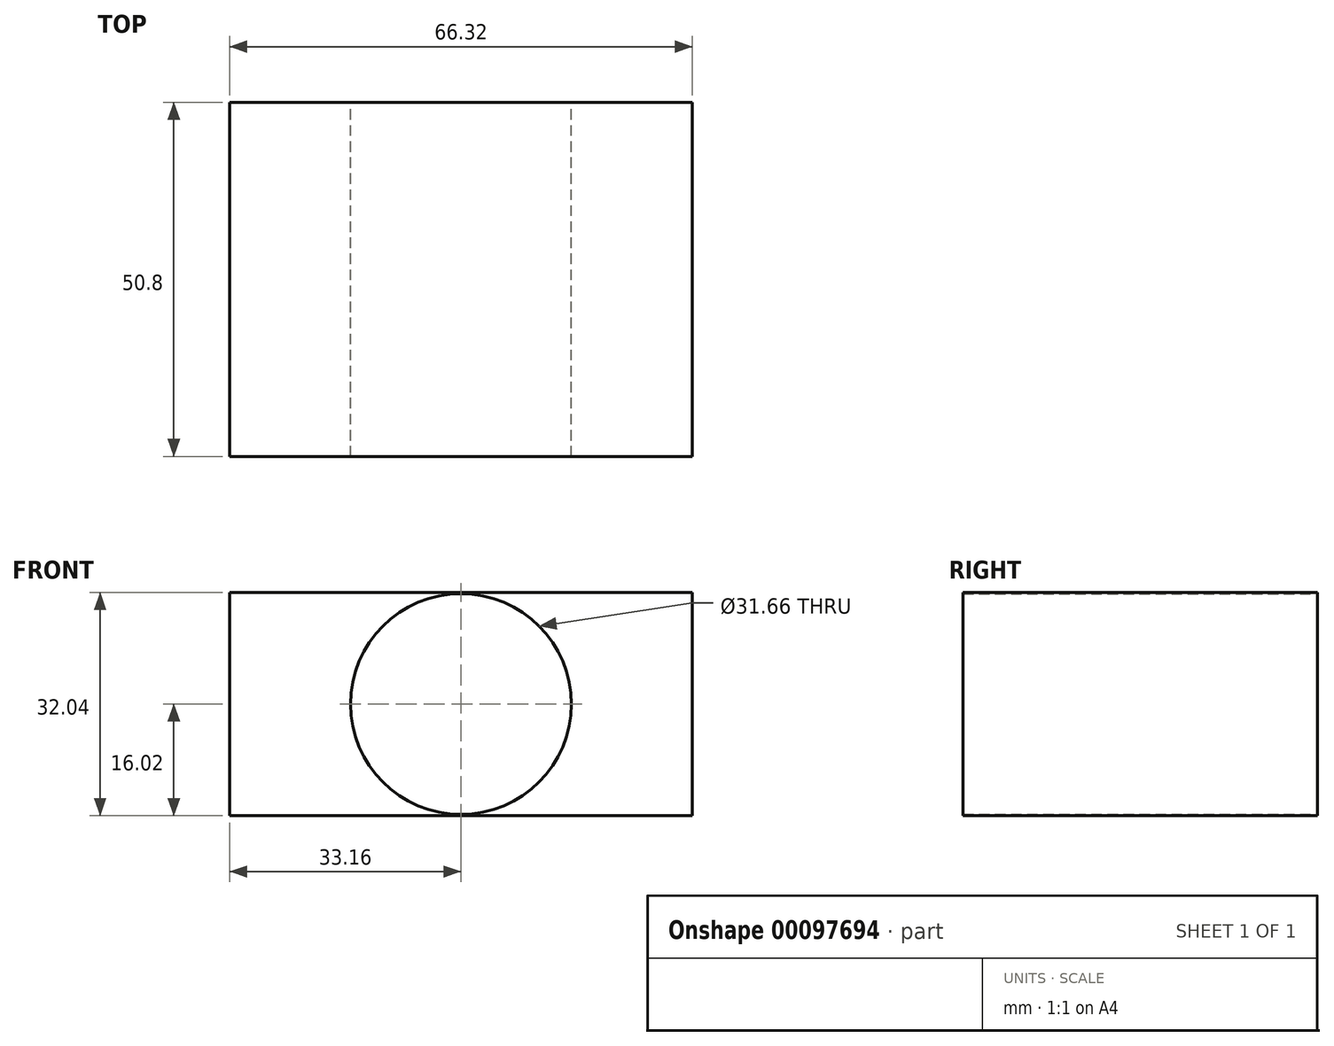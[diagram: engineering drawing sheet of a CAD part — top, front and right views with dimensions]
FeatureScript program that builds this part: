
annotation { "Feature Type Name" : "Feature", "Feature Type Description" : "" }
export const myFeature = defineFeature(function(context is Context, id is Id, definition is map)
    precondition{}
    {
        {
            var Q0;
            Q0=qCreatedBy(makeId("Front.planeOp"),FACE);
            var sketch = newSketch(context, id + "F0", { "sketchPlane" : qUnion([Q0])});
            skLineSegment(sketch, "E0.bottom", {"start": v(33.16, -16.02) * mm, "end": v(-33.16, -16.02) * mm});
            skLineSegment(sketch, "E0.top", {"start": v(33.16, 16.02) * mm, "end": v(-33.16, 16.02) * mm});
            skLineSegment(sketch, "E0.left", {"start": v(33.16, -16.02) * mm, "end": v(33.16, 16.02) * mm});
            skLineSegment(sketch, "E0.right", {"start": v(-33.16, -16.02) * mm, "end": v(-33.16, 16.02) * mm});
            skPoint(sketch, "E0.middle", {"position": v(0, 0) * mm});
            skCircle(sketch, "E1", {"center": v(0, 0) * mm, "radius": 15.83 * mm});
            skSolve(sketch);
        }
        {
            var Q0;
            Q0 = qSketchRegion(id + "F0", true);
            extrude(context, id + "F1", {"entities" : qUnion([Q0]), "endBound" : BoundingType.SYMMETRIC, "depth" : 50.8 * mm});
        }
    });
